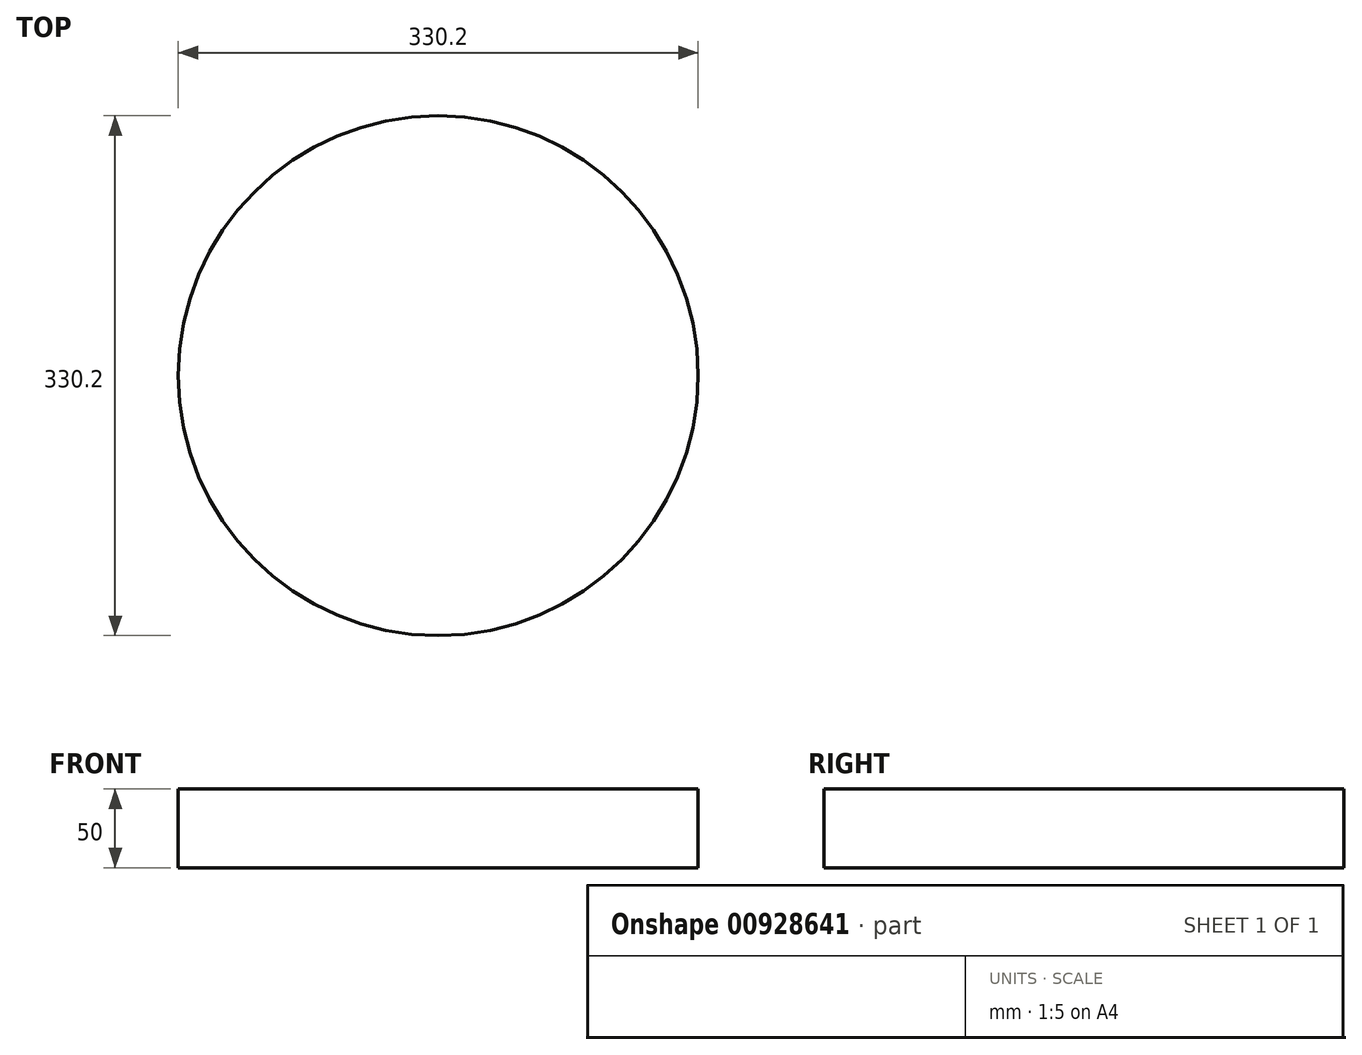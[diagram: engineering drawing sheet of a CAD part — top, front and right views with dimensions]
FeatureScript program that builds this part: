
annotation { "Feature Type Name" : "Feature", "Feature Type Description" : "" }
export const myFeature = defineFeature(function(context is Context, id is Id, definition is map)
    precondition{}
    {
        {
            var Q0;
            Q0=qCreatedBy(makeId("Top.planeOp"),FACE);
            var sketch = newSketch(context, id + "F0", { "sketchPlane" : qUnion([Q0])});
            skCircle(sketch, "E0", {"center": v(0, 0) * mm, "radius": 165.1 * mm});
            skSolve(sketch);
        }
        {
            var Q0;
            Q0 = qSketchRegion(id + "F0", true);
            extrude(context, id + "F1", {"entities" : qUnion([Q0]), "depth" : 50 * mm, "offsetDistance" : 25.4 * mm});
        }
    });
